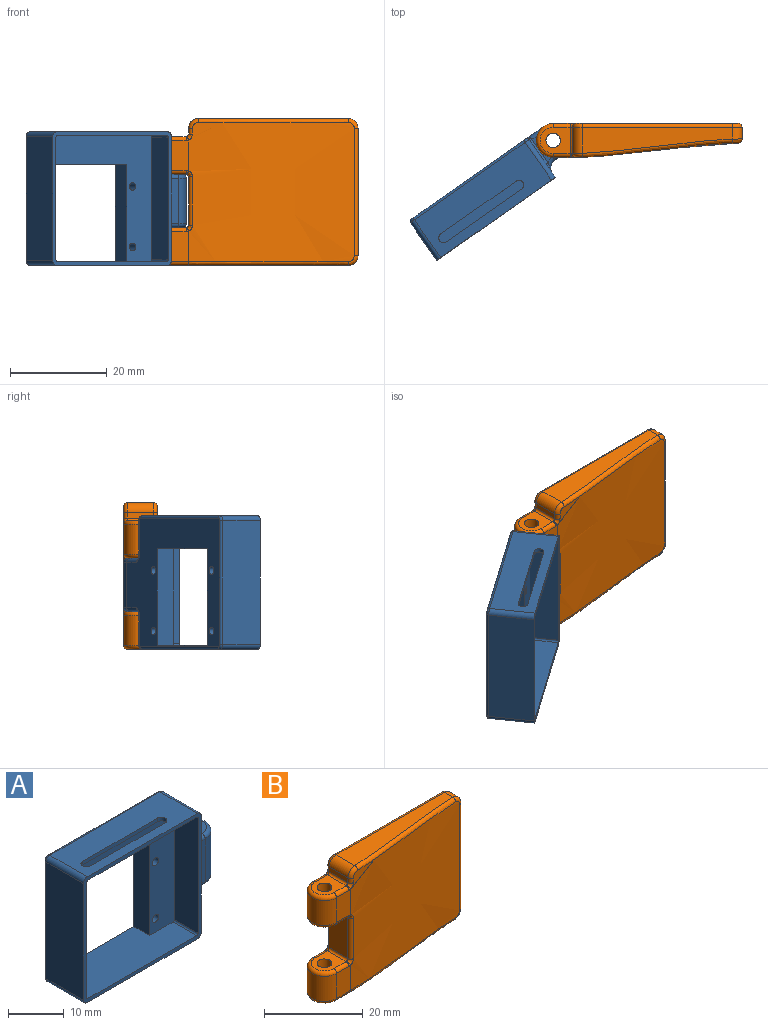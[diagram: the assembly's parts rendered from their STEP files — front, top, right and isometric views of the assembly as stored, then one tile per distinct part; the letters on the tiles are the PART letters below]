
ASSEMBLY  parts=2 mates=1
PART A: 61 faces, bbox 37.8x11x27.8 mm
  f0: plane 18x4mm, normal (0,0,-1), area 72mm2, adj f1,f6,f7,f8
  f1: plane 20x4mm, normal (-1,0,0), area 80mm2, adj f0,f7,f8,f12
  f2: cylinder r=0.8mm len=4mm, axis (0,1,0), area 20.1mm2, adj f7,f8
  f3: cylinder r=0.8mm len=4mm, axis (0,1,0), area 20.1mm2, adj f7,f8
  f4: cylinder r=0.8mm len=4mm, axis (0,1,0), area 20.1mm2, adj f7,f8
  f5: cylinder r=0.8mm len=4mm, axis (0,1,0), area 20.1mm2, adj f7,f8
  f6: plane 20x4mm, normal (1,0,0), area 80mm2, adj f0,f7,f8,f12
  f7: plane 28.3x26mm, normal (0,-1,0), area 367.7mm2, adj f0,f1,f2,f3,f4,f5,f6,f9
  f8: plane 33.4x26.6mm, normal (0,1,0), area 443.5mm2, adj f0,f1,f2,f3,f4,f5,f6,f12
  f9: plane 25.3x6mm, normal (-1,0,0), area 151.8mm2, adj f7,f17,f28,f29
  f10: plane 27.6x6mm, normal (0,0,-1), area 124.5mm2, adj f7,f17,f18,f19,f20,f21,f27,f28
  f11: plane 25.3x6mm, normal (1,0,0), area 151.8mm2, adj f7,f17,f26,f27
  f12: plane 27.6x10mm, normal (0,0,1), area 237.6mm2, adj f1,f6,f7,f8,f17,f26,f29
  f13: plane 25.6x9.5mm, normal (1,0,0), area 143.4mm2, adj f17,f22,f25,f35,f44,f45,f46,f47
  f14: plane 27.9x9.5mm, normal (0,0,1), area 223.9mm2, adj f17,f18,f19,f20,f21,f22,f23,f53
  f15: plane 25.6x9.5mm, normal (-1,0,0), area 243.2mm2, adj f17,f23,f24,f55
  f16: plane 27.9x9.5mm, normal (0,0,-1), area 265mm2, adj f17,f24,f25,f57
  f17: plane 29.9x27.6mm, normal (0,-1,0), area 88.7mm2, adj f9,f10,f11,f12,f13,f14,f15,f16
  f18: plane 19x0.8mm, normal (0,-1,0), area 15.2mm2, adj f10,f14,f20,f21
  f19: plane 19x0.8mm, normal (0,1,0), area 15.2mm2, adj f10,f14,f20,f21
  f20: cylinder r=1mm len=2mm, axis (0,0,-1), area 2.5mm2, adj f10,f14,f18,f19
  f21: cylinder r=1mm len=2mm, axis (0,0,1), area 2.5mm2, adj f10,f14,f18,f19
  f22: cylinder r=1mm len=9.5mm, axis (0,1,0), area 14.9mm2, adj f13,f14,f17,f52
  f23: cylinder r=1mm len=9.5mm, axis (0,-1,0), area 14.9mm2, adj f14,f15,f17,f54
  f24: cylinder r=1mm len=9.5mm, axis (0,1,0), area 14.9mm2, adj f15,f16,f17,f56
  f25: cylinder r=1mm len=9.5mm, axis (0,-1,0), area 14.9mm2, adj f13,f16,f17,f58
  f26: cylinder r=0.35mm len=6mm, axis (0,-1,0), area 3.3mm2, adj f7,f11,f12,f17
  f27: cylinder r=0.35mm len=6mm, axis (0,1,0), area 3.3mm2, adj f7,f10,f11,f17
  f28: cylinder r=0.35mm len=6mm, axis (0,-1,0), area 3.3mm2, adj f7,f9,f10,f17
  f29: cylinder r=0.35mm len=6mm, axis (0,1,0), area 3.3mm2, adj f7,f9,f12,f17
  f30: plane 9.4x2mm, normal (0,-1,0), area 18.8mm2, adj f31,f35,f37,f41
  f31: cylinder r=3.5mm len=9.4mm, axis (0,0,-1), area 103.4mm2, adj f8,f30,f38,f42
  f32: cylinder r=1.5mm len=11mm, axis (0,0,-1), area 103.7mm2, adj f33,f34
  f33: plane 6.2x5.84mm, normal (0,0,1), area 23.5mm2, adj f32,f40,f41,f42,f43,f45
  f34: plane 6.2x5.84mm, normal (0,0,-1), area 23.5mm2, adj f32,f36,f37,f38,f39,f48
  f35: cylinder r=2mm len=9.4mm, axis (0,0,1), area 29.5mm2, adj f13,f30,f36,f40
  f36: torus R=2.8mm, axis (0,0,1), area 2.7mm2, adj f34,f35,f37,f47
  f37: cylinder r=0.8mm len=2mm, axis (1,0,0), area 2.5mm2, adj f30,f34,f36,f38
  f38: torus R=2.7mm, axis (0,0,1), area 12.7mm2, adj f31,f34,f37,f39
  f39: cylinder r=0.8mm len=3.5mm, axis (-1,0,0), area 4.4mm2, adj f8,f34,f38,f49
  f40: torus R=2.8mm, axis (0,0,1), area 2.7mm2, adj f33,f35,f41,f44
  f41: cylinder r=0.8mm len=2mm, axis (-1,0,0), area 2.5mm2, adj f30,f33,f40,f42
  f42: torus R=2.7mm, axis (0,0,1), area 12.7mm2, adj f31,f33,f41,f43
  f43: cylinder r=0.8mm len=3.5mm, axis (1,0,0), area 4.4mm2, adj f8,f33,f42,f46
  f44: bspline ~2.36x1.3mm, area 1.1mm2, adj f13,f40,f45
  f45: cylinder r=0.5mm len=5.84mm, axis (0,1,0), area 4.6mm2, adj f13,f33,f44,f46
  f46: torus R=1.3mm, axis (1,0,0), area 0.5mm2, adj f13,f43,f45,f50
  f47: bspline ~2.73x1.3mm, area 1.1mm2, adj f13,f36,f48
  f48: cylinder r=0.5mm len=5.84mm, axis (0,-1,0), area 4.6mm2, adj f13,f34,f47,f49
  f49: torus R=1.3mm, axis (1,0,0), area 0.5mm2, adj f13,f39,f48,f60
  f50: bspline ~1.48x1mm, area 0.7mm2, adj f8,f46,f51
  f51: cylinder r=0.5mm len=7.34mm, axis (0,0,1), area 5.8mm2, adj f8,f13,f50,f52
  f52: torus R=0.5mm, axis (0,-1,0), area 1mm2, adj f8,f22,f51,f53
  f53: cylinder r=0.5mm len=27.9mm, axis (-1,0,0), area 21.9mm2, adj f8,f14,f52,f54
  f54: torus R=0.5mm, axis (0,-1,0), area 1mm2, adj f8,f23,f53,f55
  f55: cylinder r=0.5mm len=25.6mm, axis (0,0,-1), area 20.1mm2, adj f8,f15,f54,f56
  f56: torus R=0.5mm, axis (0,-1,0), area 1mm2, adj f8,f24,f55,f57
  f57: cylinder r=0.5mm len=27.9mm, axis (1,0,0), area 21.9mm2, adj f8,f16,f56,f58
  f58: torus R=0.5mm, axis (0,-1,0), area 1mm2, adj f8,f25,f57,f59
  f59: cylinder r=0.5mm len=6.34mm, axis (0,0,1), area 5mm2, adj f8,f13,f58,f60
  f60: bspline ~1.48x1mm, area 0.7mm2, adj f8,f49,f59
PART B: 58 faces, bbox 43x7.6x30.6 mm
  f0: plane 6.28x4mm, normal (0,-1,0), area 24.7mm2, adj f3,f10,f34,f35,f39
  f1: cylinder r=1.5mm len=7.78mm, axis (0,0,-1), area 73.3mm2, adj f8,f15
  f2: plane 38.2x28.7mm, normal (0,1,0), area 1018mm2, adj f3,f4,f22,f24,f26,f28,f30,f36
  f3: cylinder r=3.5mm len=7mm, axis (0,0,-1), area 67.9mm2, adj f0,f2,f32,f37
  f4: cylinder r=3.5mm len=7mm, axis (0,0,-1), area 67.9mm2, adj f2,f5,f23,f54
  f5: plane 6.38x4mm, normal (0,-1,0), area 24.7mm2, adj f4,f10,f25,f27,f56,f57
  f6: cylinder r=1.5mm len=7.78mm, axis (0,0,-1), area 73.3mm2, adj f7,f14
  f7: plane 6.2x5.4mm, normal (0,0,1), area 23.3mm2, adj f6,f18,f52,f54,f56
  f8: plane 39.7x5.4mm, normal (0,0,-1), area 157.5mm2, adj f1,f19,f36,f37,f39,f41
  f9: plane 5.4x1.2mm, normal (-1,0,0), area 6.5mm2, adj f18,f20,f48,f53
  f10: extruded ~34.21x28.7mm, area 972.4mm2, adj f0,f5,f29,f31,f33,f41,f43,f45
  f11: plane 26.3x2.4mm, normal (1,0,0), area 63.2mm2, adj f19,f21,f40,f45
  f12: plane 31x5.37mm, normal (0,0,1), area 120.8mm2, adj f20,f21,f44,f49
  f13: plane 10.05x5.4mm, normal (-1,0,0), area 54.2mm2, adj f16,f17,f26,f31
  f14: plane 6.2x5.4mm, normal (0,0,-1), area 23.3mm2, adj f6,f17,f22,f23,f25
  f15: plane 6.2x5.4mm, normal (0,0,1), area 23.3mm2, adj f1,f16,f30,f32,f34
  f16: cylinder r=0.5mm len=5.4mm, axis (0,-1,0), area 4.2mm2, adj f13,f15,f28,f33,f35
  f17: cylinder r=0.5mm len=5.4mm, axis (0,1,0), area 4.2mm2, adj f13,f14,f24,f27,f29
  f18: cylinder r=0.5mm len=5.4mm, axis (0,1,0), area 4.2mm2, adj f7,f9,f50,f55,f57
  f19: cylinder r=2mm len=2.43mm, axis (0,1,0), area 7.6mm2, adj f8,f11,f38,f43
  f20: cylinder r=2mm len=5.4mm, axis (0,1,0), area 16.9mm2, adj f9,f12,f46,f51
  f21: cylinder r=2mm len=2.43mm, axis (0,-1,0), area 7.6mm2, adj f11,f12,f42,f47
  f22: cylinder r=0.8mm len=3.5mm, axis (-1,0,0), area 4.4mm2, adj f2,f14,f23,f24
  f23: torus R=2.7mm, axis (0,0,1), area 12.7mm2, adj f4,f14,f22,f25
  f24: torus R=1.3mm, axis (0,1,0), area 1.6mm2, adj f2,f17,f22,f26
  f25: cylinder r=0.8mm len=3.5mm, axis (1,0,0), area 4.4mm2, adj f5,f14,f23,f27
  f26: cylinder r=0.8mm len=10.05mm, axis (0,0,-1), area 12.6mm2, adj f2,f13,f24,f28
  f27: torus R=1.3mm, axis (0,1,0), area 0.4mm2, adj f5,f17,f25,f29
  f28: torus R=1.3mm, axis (0,1,0), area 1.6mm2, adj f2,f16,f26,f30
  f29: bspline ~1.41x1.15mm, area 1.2mm2, adj f10,f17,f27,f31
  f30: cylinder r=0.8mm len=3.5mm, axis (1,0,0), area 4.4mm2, adj f2,f15,f28,f32
  f31: cylinder r=0.8mm len=10.05mm, axis (0,0,-1), area 12.7mm2, adj f10,f13,f29,f33
  f32: torus R=2.7mm, axis (0,0,1), area 12.7mm2, adj f3,f15,f30,f34
  f33: bspline ~1.41x1.15mm, area 1.2mm2, adj f10,f16,f31,f35
  f34: cylinder r=0.8mm len=3.5mm, axis (-1,0,0), area 4.4mm2, adj f0,f15,f32,f35
  f35: torus R=1.3mm, axis (0,1,0), area 0.4mm2, adj f0,f16,f33,f34
  f36: cylinder r=0.8mm len=37mm, axis (-1,0,0), area 46.5mm2, adj f2,f8,f37,f38
  f37: torus R=2.7mm, axis (0,0,1), area 12.7mm2, adj f3,f8,f36,f39
  f38: torus R=1.2mm, axis (0,1,0), area 3.4mm2, adj f2,f19,f36,f40
  f39: cylinder r=0.8mm len=4mm, axis (1,0,0), area 5mm2, adj f0,f8,f37,f41
  f40: cylinder r=0.8mm len=26.3mm, axis (0,0,-1), area 33mm2, adj f2,f11,f38,f42
  f41: bspline ~41.04x3.79mm, area 41.7mm2, adj f8,f10,f39,f43
  f42: torus R=1.2mm, axis (0,1,0), area 3.4mm2, adj f2,f21,f40,f44
  f43: bspline ~2.45x2.45mm, area 3.3mm2, adj f10,f19,f41,f45
  f44: cylinder r=0.8mm len=31mm, axis (1,0,0), area 39mm2, adj f2,f12,f42,f46
  f45: cylinder r=0.8mm len=26.3mm, axis (0,0,-1), area 32.8mm2, adj f10,f11,f43,f47
  f46: torus R=1.2mm, axis (0,1,0), area 3.4mm2, adj f2,f20,f44,f48
  f47: bspline ~2.45x2.45mm, area 3.3mm2, adj f10,f21,f45,f49
  f48: cylinder r=0.8mm len=1.2mm, axis (0,0,1), area 1.5mm2, adj f2,f9,f46,f50
  f49: bspline ~32.8x3.78mm, area 39.1mm2, adj f10,f12,f47,f51
  f50: torus R=1.3mm, axis (0,1,0), area 1.6mm2, adj f2,f18,f48,f52
  f51: bspline ~2.47x2.45mm, area 3.4mm2, adj f10,f20,f49,f53
  f52: cylinder r=0.8mm len=3.5mm, axis (1,0,0), area 4.4mm2, adj f2,f7,f50,f54
  f53: cylinder r=0.8mm len=1.2mm, axis (0,0,-1), area 1.5mm2, adj f9,f10,f51,f55
  f54: torus R=2.7mm, axis (0,0,1), area 12.7mm2, adj f4,f7,f52,f56
  f55: bspline ~1.41x1.15mm, area 1.2mm2, adj f10,f18,f53,f57
  f56: cylinder r=0.8mm len=3.5mm, axis (-1,0,0), area 4.4mm2, adj f5,f7,f54,f57
  f57: torus R=1.3mm, axis (0,1,0), area 0.4mm2, adj f5,f18,f55,f56
PLACE A rot(axis=(0,0,1),35deg) t=(-33.12,-19.62,-12.5)mm
PLACE B at identity fixed
MATE revolute A.f31 <-> B.f1  axis (0,0,-1) through (-4,-3.5,0)mm
